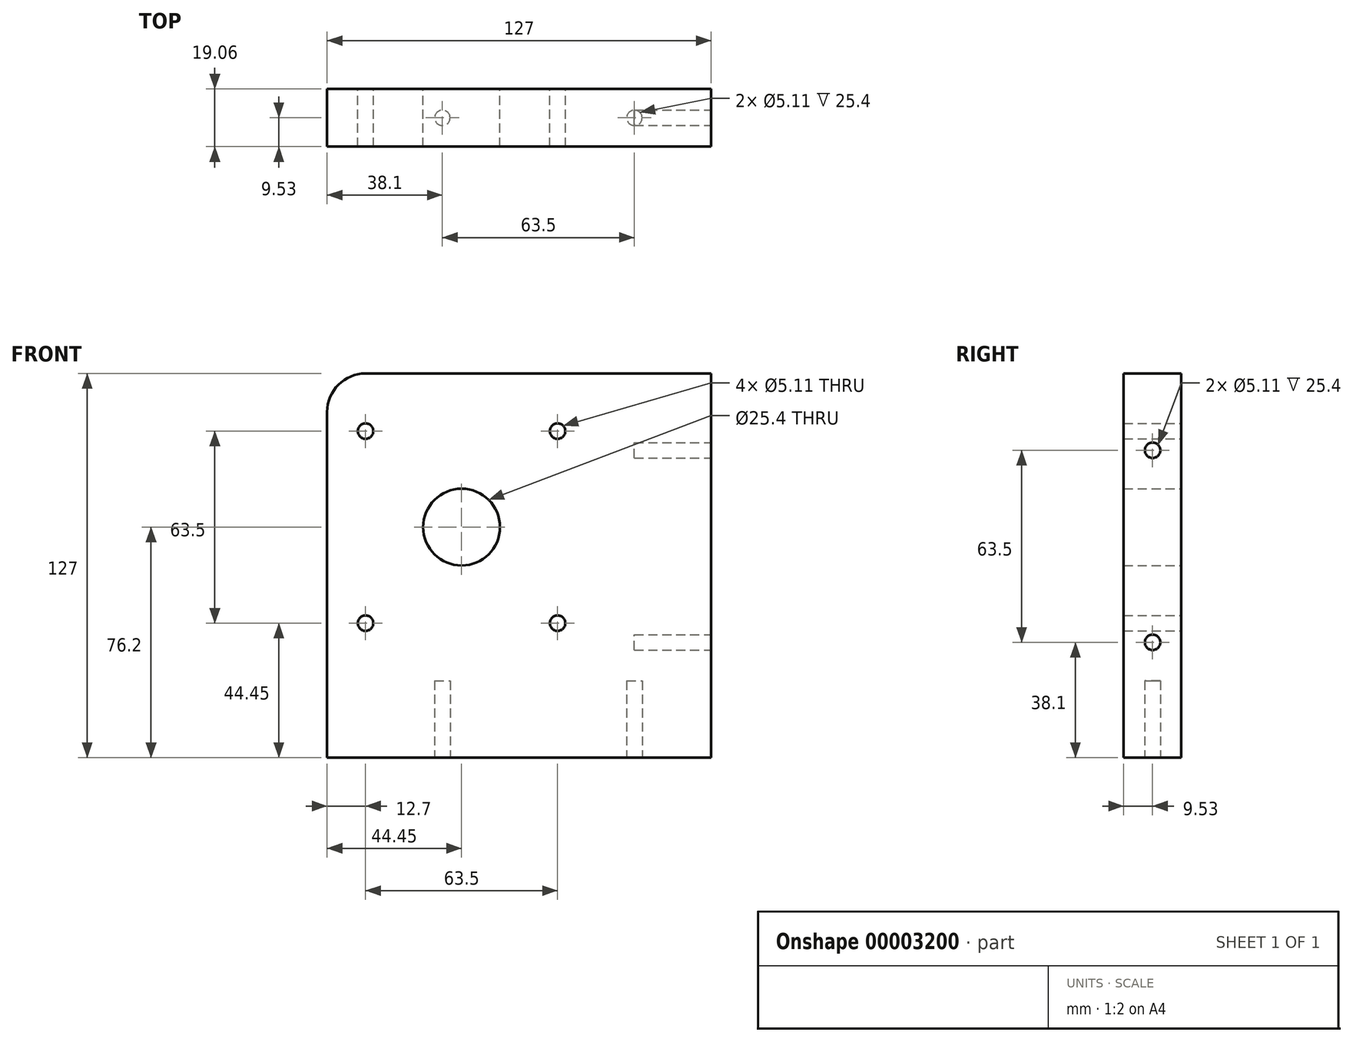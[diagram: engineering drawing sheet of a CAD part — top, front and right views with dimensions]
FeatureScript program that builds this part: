
annotation { "Feature Type Name" : "Feature", "Feature Type Description" : "" }
export const myFeature = defineFeature(function(context is Context, id is Id, definition is map)
    precondition{}
    {
        {
            var Q0;
            Q0=qCreatedBy(makeId("Front.planeOp"),FACE);
            var sketch = newSketch(context, id + "F0", { "sketchPlane" : qUnion([Q0])});
            skLineSegment(sketch, "E0", {"start": v(0, 0) * mm, "end": v(0, -127) * mm});
            skLineSegment(sketch, "E1", {"start": v(0, -127) * mm, "end": v(127, -127) * mm});
            skLineSegment(sketch, "E2", {"start": v(127, -127) * mm, "end": v(127, 0) * mm});
            skLineSegment(sketch, "E3", {"start": v(127, 0) * mm, "end": v(0, 0) * mm});
            skLineSegment(sketch, "E4", {"start": v(12.7, 0) * mm, "end": v(12.7, -127) * mm, "construction": true});
            skLineSegment(sketch, "E5", {"start": v(76.2, 0) * mm, "end": v(76.2, -127) * mm, "construction": true});
            skLineSegment(sketch, "E6", {"start": v(0, -82.55) * mm, "end": v(127, -82.55) * mm, "construction": true});
            skLineSegment(sketch, "E7", {"start": v(0, -19.05) * mm, "end": v(127, -19.05) * mm, "construction": true});
            skCircle(sketch, "E8", {"center": v(12.7, -19.05) * mm, "radius": 2.55 * mm});
            skCircle(sketch, "E9", {"center": v(76.2, -19.05) * mm, "radius": 2.55 * mm});
            skCircle(sketch, "E10", {"center": v(76.2, -82.55) * mm, "radius": 2.55 * mm});
            skCircle(sketch, "E11", {"center": v(12.7, -82.55) * mm, "radius": 2.55 * mm});
            skLineSegment(sketch, "E12", {"start": v(44.45, 0) * mm, "end": v(44.45, -127) * mm, "construction": true});
            skLineSegment(sketch, "E13", {"start": v(127, -50.8) * mm, "end": v(12.7, -50.8) * mm, "construction": true});
            skCircle(sketch, "E14", {"center": v(44.45, -50.8) * mm, "radius": 12.7 * mm});
            skSolve(sketch);
        }
        {
            var Q0;
            Q0=qSketchRegion(id+"F0",true);
            extrude(context, id + "F1", {"entities" : qUnion([Q0]), "endBound" : BoundingType.SYMMETRIC, "depth" : 19.05 * mm});
        }
        {
            var Q0;
            Q0=makeQuery(id+"F1.opExtrude","SWEPT_FACE",FACE,{"disambiguationData":[OSD([sQuery(id+"F0.wireOp",EDGE,"E1")])]});
            var sketch = newSketch(context, id + "F2", { "sketchPlane" : qUnion([Q0])});
            skLineSegment(sketch, "E15", {"start": v(0, 0) * mm, "end": v(127, 0) * mm, "construction": true});
            skLineSegment(sketch, "E16", {"start": v(38.1, 9.53) * mm, "end": v(38.1, -9.53) * mm, "construction": true});
            skLineSegment(sketch, "E17", {"start": v(101.6, 9.53) * mm, "end": v(101.6, -9.53) * mm, "construction": true});
            skCircle(sketch, "E18", {"center": v(38.1, 0) * mm, "radius": 2.55 * mm});
            skCircle(sketch, "E19", {"center": v(101.6, 0) * mm, "radius": 2.55 * mm});
            skSolve(sketch);
        }
        {
            var Q0;
            Q0=qSketchRegion(id+"F2",true);
            extrude(context, id + "F3", {"entities" : qUnion([Q0]), "operationType" : NewBodyOperationType.REMOVE, "oppositeDirection" : true, "depth" : 25.4 * mm});
        }
        {
            var Q0;
            Q0=makeQuery(id+"F1.opExtrude","SWEPT_FACE",FACE,{"disambiguationData":[OSD([sQuery(id+"F0.wireOp",EDGE,"E2")])]});
            var sketch = newSketch(context, id + "F4", { "sketchPlane" : qUnion([Q0])});
            skLineSegment(sketch, "E20", {"start": v(0, 0) * mm, "end": v(0, -127) * mm, "construction": true});
            skLineSegment(sketch, "E21", {"start": v(9.53, -25.4) * mm, "end": v(-9.53, -25.4) * mm, "construction": true});
            skLineSegment(sketch, "E22", {"start": v(9.53, -88.9) * mm, "end": v(-9.53, -88.9) * mm, "construction": true});
            skCircle(sketch, "E23", {"center": v(0, -25.4) * mm, "radius": 2.55 * mm});
            skCircle(sketch, "E24", {"center": v(0, -88.9) * mm, "radius": 2.55 * mm});
            skSolve(sketch);
        }
        {
            var Q0;
            Q0=qSketchRegion(id+"F4",true);
            extrude(context, id + "F5", {"entities" : qUnion([Q0]), "operationType" : NewBodyOperationType.REMOVE, "oppositeDirection" : true, "depth" : 25.4 * mm});
        }
        {
            var Q0;
            Q0=makeQuery(id+"F1.opExtrude","SWEPT_EDGE",EDGE,{"disambiguationData":[OSD([sQuery(id+"F0.wireOp",EDGE,"E0"),sQuery(id+"F0.wireOp",EDGE,"E3")])]});
            fillet(context, id + "F6", {"entities" : qUnion([Q0]), "radius" : 12.7 * mm, "tangentPropagation" : true, "allowEdgeOverflow" : false});
        }
    });
